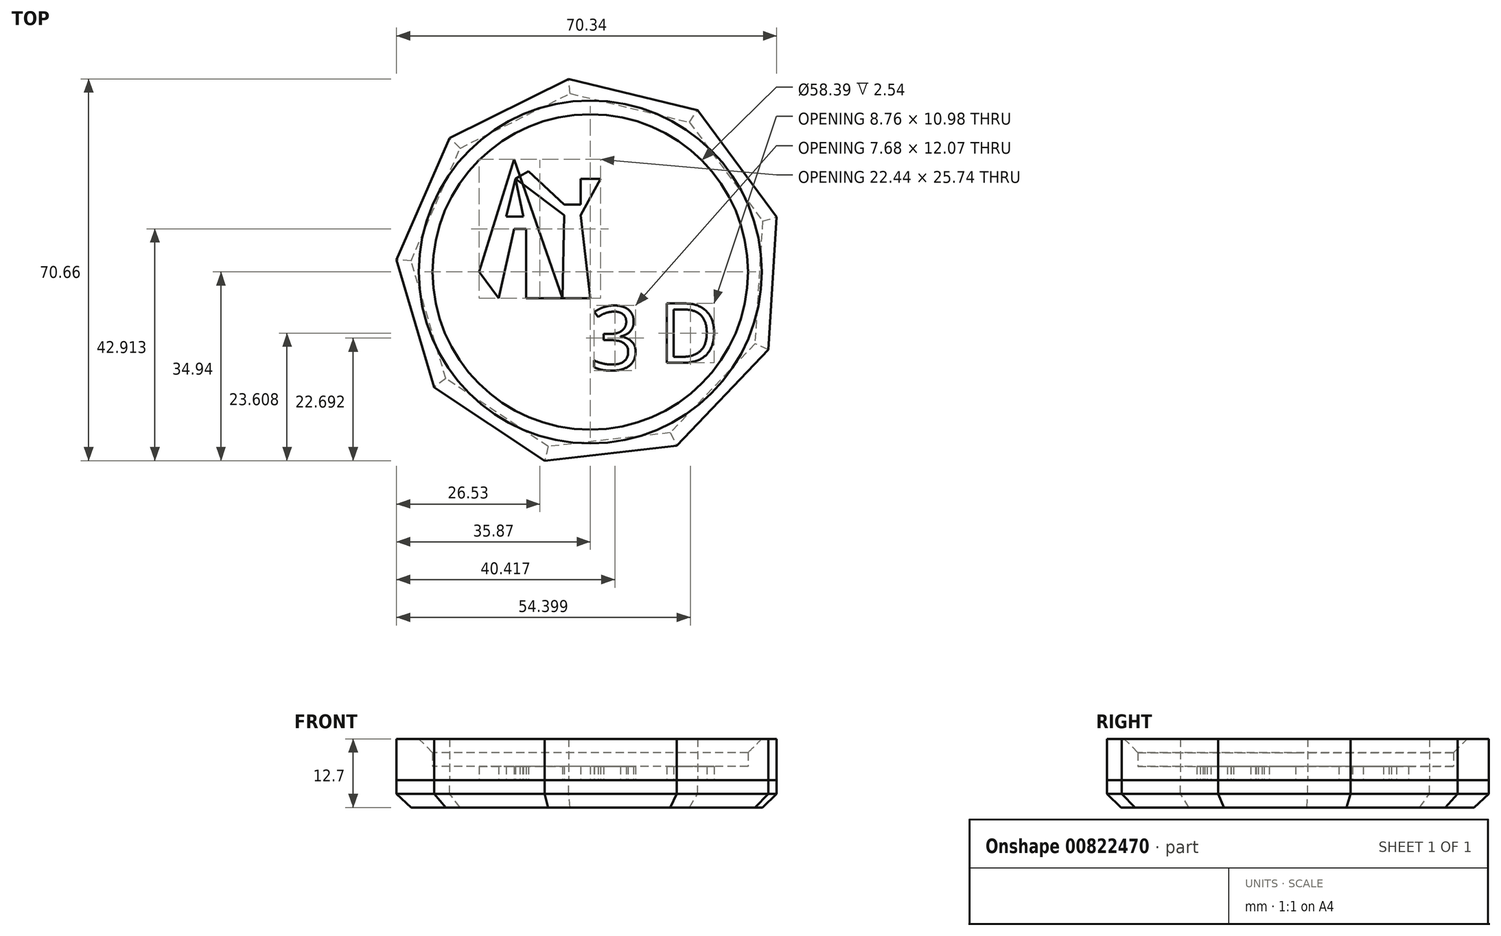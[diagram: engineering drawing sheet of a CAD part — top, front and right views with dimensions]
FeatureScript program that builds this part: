
annotation { "Feature Type Name" : "Feature", "Feature Type Description" : "" }
export const myFeature = defineFeature(function(context is Context, id is Id, definition is map)
    precondition{}
    {
        {
            var Q0;
            Q0=qCreatedBy(makeId("Top.planeOp"),FACE);
            var sketch = newSketch(context, id + "F0", { "sketchPlane" : qUnion([Q0])});
            skCircle(sketch, "E0", {"center": v(0, 0) * mm, "radius": 29.2 * mm});
            skCircle(sketch, "E1.cCircle", {"center": v(0, 0) * mm, "radius": 33.78 * mm, "construction": true});
            skLineSegment(sketch, "E1.0", {"start": v(34.47, 10.17) * mm, "end": v(32.95, -14.37) * mm});
            skLineSegment(sketch, "E1.1", {"start": v(32.95, -14.37) * mm, "end": v(16, -32.18) * mm});
            skLineSegment(sketch, "E1.2", {"start": v(16, -32.18) * mm, "end": v(-8.43, -34.94) * mm});
            skLineSegment(sketch, "E1.3", {"start": v(-8.43, -34.94) * mm, "end": v(-28.92, -21.35) * mm});
            skLineSegment(sketch, "E1.4", {"start": v(-28.92, -21.35) * mm, "end": v(-35.87, 2.23) * mm});
            skLineSegment(sketch, "E1.5", {"start": v(-35.87, 2.23) * mm, "end": v(-26.05, 24.77) * mm});
            skLineSegment(sketch, "E1.6", {"start": v(-26.05, 24.77) * mm, "end": v(-4.03, 35.72) * mm});
            skLineSegment(sketch, "E1.7", {"start": v(-4.03, 35.72) * mm, "end": v(19.87, 29.95) * mm});
            skLineSegment(sketch, "E1.8", {"start": v(19.87, 29.95) * mm, "end": v(34.47, 10.17) * mm});
            skPoint(sketch, "E1.0.midPoint", {"position": v(33.71, -2.1) * mm});
            skLineSegment(sketch, "E2", {"start": v(-20.56, 0) * mm, "end": v(-14.13, 20.84) * mm});
            skLineSegment(sketch, "E3", {"start": v(-14.13, 20.84) * mm, "end": v(-5.18, -4.9) * mm});
            skLineSegment(sketch, "E4", {"start": v(-5.18, -4.9) * mm, "end": v(-11.89, -4.9) * mm});
            skLineSegment(sketch, "E5", {"start": v(-11.89, -4.9) * mm, "end": v(-11.89, 7.97) * mm});
            skPoint(sketch, "E5.endSnap0", {"position": v(-9.65, 7.97) * mm});
            skLineSegment(sketch, "E6", {"start": v(-11.89, 7.97) * mm, "end": v(-14.13, 7.97) * mm});
            skLineSegment(sketch, "E7", {"start": v(-14.13, 7.97) * mm, "end": v(-16.93, -4.9) * mm});
            skLineSegment(sketch, "E8", {"start": v(-16.93, -4.9) * mm, "end": v(-20.56, 0) * mm});
            skLineSegment(sketch, "E9", {"start": v(-12.4, 10.24) * mm, "end": v(-15.58, 10.24) * mm});
            skLineSegment(sketch, "E10", {"start": v(-15.58, 10.24) * mm, "end": v(-13.87, 17.26) * mm});
            skLineSegment(sketch, "E11", {"start": v(-13.87, 17.26) * mm, "end": v(-12.4, 10.24) * mm});
            skLineSegment(sketch, "E12", {"start": v(-13.87, 17.26) * mm, "end": v(-4.83, 10.52) * mm});
            skLineSegment(sketch, "E13", {"start": v(-4.83, 10.52) * mm, "end": v(-5.18, -4.9) * mm});
            skLineSegment(sketch, "E14", {"start": v(0, -4.9) * mm, "end": v(-5.18, -4.9) * mm});
            skLineSegment(sketch, "E15", {"start": v(0, -4.9) * mm, "end": v(-1.8, 10.52) * mm});
            skLineSegment(sketch, "E16", {"start": v(-1.8, 10.52) * mm, "end": v(1.88, 17.26) * mm});
            skLineSegment(sketch, "E17", {"start": v(1.88, 17.26) * mm, "end": v(-1.8, 17.26) * mm});
            skLineSegment(sketch, "E18", {"start": v(-1.8, 17.26) * mm, "end": v(-1.8, 12.46) * mm});
            skLineSegment(sketch, "E19", {"start": v(-1.8, 12.46) * mm, "end": v(-4.83, 12.46) * mm});
            skLineSegment(sketch, "E20", {"start": v(-4.83, 12.46) * mm, "end": v(-11.43, 18.63) * mm});
            skLineSegment(sketch, "E21", {"start": v(-11.43, 18.63) * mm, "end": v(-13.87, 17.26) * mm});
            skText(sketch, "E22", { "text": "3", "fontName": "OpenSans-Regular.ttf"});
            skText(sketch, "E23", { "text": "D", "fontName": "OpenSans-Regular.ttf"});
            const initialGuessF0  = {"E22": [-5e-05, -0.01812, 1, 0, 0.01184], "E23": [0.01264, -0.01682, 1, 0, 0.01107]};
            skSetInitialGuess(sketch, initialGuessF0);
            skSolve(sketch);
        }
        {
            var Q0;
            Q0=makeQuery(id+"F0.imprint","IMPRINT",FACE,{"disambiguationData":[TD([[makeQuery(id+"F0.imprint","IMPRINT",EDGE,{"derivedFrom":sQuery(id+"F0.wireOp",EDGE,"E0")}),-1.0]])]});
            extrude(context, id + "F1", {"entities" : qUnion([Q0]), "depth" : 7.62 * mm, "offsetDistance" : 25.4 * mm});
        }
        {
            var Q0;
            Q0=makeQuery(id+"F0.imprint","IMPRINT",FACE,{"disambiguationData":[TD([[makeQuery(id+"F0.imprint","IMPRINT",EDGE,{"derivedFrom":sQuery(id+"F0.wireOp",EDGE,"E0")}),1.0]])]});
            var Q1;
            {var subQ0=sQuery(id+"F0.wireOp",EDGE,"E13");Q1=makeQuery(id+"F0.imprint","IMPRINT",FACE,{"disambiguationData":[TD([[makeQuery(id+"F0.imprint","IMPRINT",EDGE,{"derivedFrom":subQ0}),-1.0]])]});}
            var Q2;
            Q2=makeQuery(id+"F0.imprint","IMPRINT",FACE,{"disambiguationData":[TD([[makeQuery(id+"F0.imprint","IMPRINT",EDGE,{"derivedFrom":sQuery(id+"F0.wireOp",EDGE,"E9")}),-1.0]])]});
            var Q3;
            Q3=makeQuery(id+"F0.imprint","IMPRINT",FACE,{"disambiguationData":[TD([[makeQuery(id+"F0.imprint","IMPRINT",EDGE,{"derivedFrom":sQuery(id+"F0.wireOp",EDGE,"E23.sketch_text.stroke-7")}),1.0]])]});
            extrude(context, id + "F2", {"entities" : qUnion([Q0, Q1, Q2, Q3]), "operationType" : NewBodyOperationType.ADD, "depth" : 2.54 * mm, "offsetDistance" : 25.4 * mm});
        }
        {
            var Q0;
            Q0=makeQuery(id+"F1.opExtrude","CAP_EDGE",EDGE,{"disambiguationData":[OSD([sQuery(id+"F0.wireOp",EDGE,"E0")])],"isStart":false});
            chamfer(context, id + "F3", {"entities" : qUnion([Q0]), "width" : 2.54 * mm, "tangentPropagation" : true});
        }
        {
            var Q0;
            Q0=makeQuery(id+"F0.imprint","IMPRINT",FACE,{"disambiguationData":[TD([[makeQuery(id+"F0.imprint","IMPRINT",EDGE,{"derivedFrom":sQuery(id+"F0.wireOp",EDGE,"E0")}),-1.0]])]});
            var Q1;
            Q1=makeQuery(id+"F0.imprint","IMPRINT",FACE,{"disambiguationData":[TD([[makeQuery(id+"F0.imprint","IMPRINT",EDGE,{"derivedFrom":sQuery(id+"F0.wireOp",EDGE,"E0")}),1.0]])]});
            var Q2;
            Q2=makeQuery(id+"F0.imprint","IMPRINT",FACE,{"disambiguationData":[TD([[makeQuery(id+"F0.imprint","IMPRINT",EDGE,{"derivedFrom":sQuery(id+"F0.wireOp",EDGE,"E9")}),-1.0]])]});
            var Q3;
            {var subQ1=sQuery(id+"F0.wireOp",EDGE,"E2");Q3=makeQuery(id+"F0.imprint","IMPRINT",FACE,{"disambiguationData":[TD([[makeQuery(id+"F0.imprint","IMPRINT",EDGE,{"derivedFrom":subQ1}),-1.0]])]});}
            var Q4;
            {var subQ0=sQuery(id+"F0.wireOp",EDGE,"E13");Q4=makeQuery(id+"F0.imprint","IMPRINT",FACE,{"disambiguationData":[TD([[makeQuery(id+"F0.imprint","IMPRINT",EDGE,{"derivedFrom":subQ0}),-1.0]])]});}
            var Q5;
            {var subQ6=sQuery(id+"F0.wireOp",EDGE,"E13");Q5=makeQuery(id+"F0.imprint","IMPRINT",FACE,{"disambiguationData":[TD([[makeQuery(id+"F0.imprint","IMPRINT",EDGE,{"derivedFrom":subQ6}),1.0]])]});}
            var Q6;
            Q6=makeQuery(id+"F0.imprint","IMPRINT",FACE,{"disambiguationData":[TD([[makeQuery(id+"F0.imprint","IMPRINT",EDGE,{"derivedFrom":sQuery(id+"F0.wireOp",EDGE,"E22.sketch_text.stroke-0")}),-1.0]])]});
            var Q7;
            Q7=makeQuery(id+"F0.imprint","IMPRINT",FACE,{"disambiguationData":[TD([[makeQuery(id+"F0.imprint","IMPRINT",EDGE,{"derivedFrom":sQuery(id+"F0.wireOp",EDGE,"E23.sketch_text.stroke-7")}),1.0]])]});
            var Q8;
            Q8=makeQuery(id+"F0.imprint","IMPRINT",FACE,{"disambiguationData":[TD([[makeQuery(id+"F0.imprint","IMPRINT",EDGE,{"derivedFrom":sQuery(id+"F0.wireOp",EDGE,"E23.sketch_text.stroke-0")}),-1.0]])]});
            extrude(context, id + "F4", {"entities" : qUnion([Q0, Q1, Q2, Q3, Q4, Q5, Q6, Q7, Q8]), "depth" : -5.08 * mm, "offsetDistance" : 25.4 * mm});
        }
        {
            var Q0;
            Q0=makeQuery(id+"F4.opExtrude","CAP_EDGE",EDGE,{"disambiguationData":[OSD([sQuery(id+"F0.wireOp",EDGE,"E1.0")])],"isStart":false});
            var Q1;
            Q1=makeQuery(id+"F4.opExtrude","CAP_EDGE",EDGE,{"disambiguationData":[OSD([sQuery(id+"F0.wireOp",EDGE,"E1.1")])],"isStart":false});
            var Q2;
            Q2=makeQuery(id+"F4.opExtrude","CAP_EDGE",EDGE,{"disambiguationData":[OSD([sQuery(id+"F0.wireOp",EDGE,"E1.2")])],"isStart":false});
            var Q3;
            Q3=makeQuery(id+"F4.opExtrude","CAP_EDGE",EDGE,{"disambiguationData":[OSD([sQuery(id+"F0.wireOp",EDGE,"E1.3")])],"isStart":false});
            var Q4;
            Q4=makeQuery(id+"F4.opExtrude","CAP_EDGE",EDGE,{"disambiguationData":[OSD([sQuery(id+"F0.wireOp",EDGE,"E1.4")])],"isStart":false});
            var Q5;
            Q5=makeQuery(id+"F4.opExtrude","CAP_EDGE",EDGE,{"disambiguationData":[OSD([sQuery(id+"F0.wireOp",EDGE,"E1.5")])],"isStart":false});
            var Q6;
            Q6=makeQuery(id+"F4.opExtrude","CAP_EDGE",EDGE,{"disambiguationData":[OSD([sQuery(id+"F0.wireOp",EDGE,"E1.6")])],"isStart":false});
            var Q7;
            Q7=makeQuery(id+"F4.opExtrude","CAP_EDGE",EDGE,{"disambiguationData":[OSD([sQuery(id+"F0.wireOp",EDGE,"E1.7")])],"isStart":false});
            var Q8;
            Q8=makeQuery(id+"F4.opExtrude","CAP_EDGE",EDGE,{"disambiguationData":[OSD([sQuery(id+"F0.wireOp",EDGE,"E1.8")])],"isStart":false});
            chamfer(context, id + "F5", {"entities" : qUnion([Q0, Q1, Q2, Q3, Q4, Q5, Q6, Q7, Q8]), "width" : 2.54 * mm, "tangentPropagation" : true});
        }
    });
